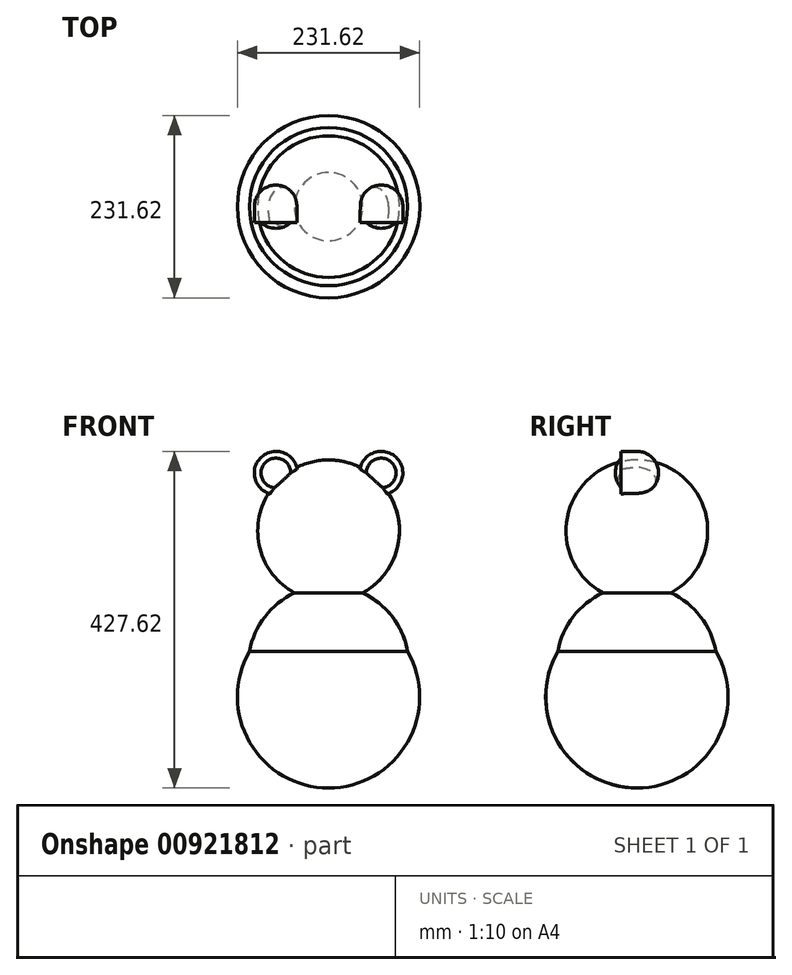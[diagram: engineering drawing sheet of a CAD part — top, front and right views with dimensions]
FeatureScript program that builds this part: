
annotation { "Feature Type Name" : "Feature", "Feature Type Description" : "" }
export const myFeature = defineFeature(function(context is Context, id is Id, definition is map)
    precondition{}
    {
        {
            var Q0;
            Q0=qCreatedBy(makeId("Front.planeOp"),FACE);
            var sketch = newSketch(context, id + "F0", { "sketchPlane" : qUnion([Q0])});
            skLineSegment(sketch, "E0", {"start": v(0, 115.17) * mm, "end": v(0, -108.63) * mm});
            skArc(sketch, "E1", {"start": v(0, 90) * mm, "mid": v(-90, 0) * mm, "end": v(0, -90) * mm});
            skSolve(sketch);
        }
        {
            var Q0;
            {var subQ0=sQuery(id+"F0.wireOp",EDGE,"mKIjtymj-Oh6m-so3v-0z2y-TkpC0XcMTjZ2");Q0=makeQuery(id+"F0.imprint","IMPRINT",FACE,{"disambiguationData":[TD([[makeQuery(id+"F0.imprint","IMPRINT",EDGE,{"derivedFrom":subQ0}),1.0]])]});}
            var Q1;
            {var subQ0=sQuery(id+"F0.wireOp",EDGE,"E1");Q1=makeQuery(id+"F0.imprint","IMPRINT",FACE,{"disambiguationData":[TD([[makeQuery(id+"F0.imprint","IMPRINT",EDGE,{"derivedFrom":subQ0}),1.0]])]});}
            var Q2;
            Q2=sQuery(id+"F0.wireOp",EDGE,"E0");
            revolve(context, id + "F1", {"surfaceOperationType" : NewSurfaceOperationType.NEW, "entities" : qUnion([Q0, Q1]), "axis" : qUnion([Q2]), "revolveType" : RevolveType.FULL});
        }
        {
            var Q0;
            Q0=qCreatedBy(makeId("Front.planeOp"),FACE);
            var sketch = newSketch(context, id + "F2", { "sketchPlane" : qUnion([Q0])});
            skCircle(sketch, "E2", {"center": v(-66.85, 73.44) * mm, "radius": 27.5 * mm});
            skLineSegment(sketch, "E3", {"start": v(0, 0) * mm, "end": v(0, 161.1) * mm});
            skCircle(sketch, "E4.MirrorC", {"center": v(66.85, 73.44) * mm, "radius": 27.5 * mm});
            skSolve(sketch);
        }
        {
            var Q0;
            Q0 = qSketchRegion(id + "F2", true);
            extrude(context, id + "F3", {"entities" : qUnion([Q0]), "operationType" : NewBodyOperationType.ADD, "depth" : 20 * mm, "offsetDistance" : 25 * mm});
        }
        {
            var Q0;
            Q0=makeQuery(id+"F3.opExtrude","CAP_FACE",FACE,{"disambiguationData":[OSD([sQuery(id+"F2.wireOp",EDGE,"E2")])],"isStart":true});
            var sketch = newSketch(context, id + "F4", { "sketchPlane" : qUnion([Q0])});
            skArc(sketch, "E5", {"start": v(66.85, 45.94) * mm, "mid": v(94.35, 73.44) * mm, "end": v(66.85, 100.94) * mm});
            skLineSegment(sketch, "E6", {"start": v(66.85, 126.85) * mm, "end": v(66.85, 15.2) * mm});
            skSolve(sketch);
        }
        {
            var Q0;
            Q0 = qSketchRegion(id + "F4", true);
            var Q1;
            Q1=sQuery(id+"F4.wireOp",EDGE,"E6");
            revolve(context, id + "F5", {"operationType" : NewBodyOperationType.ADD, "surfaceOperationType" : NewSurfaceOperationType.NEW, "entities" : qUnion([Q0]), "axis" : qUnion([Q1]), "revolveType" : RevolveType.FULL});
        }
        {
            var Q0;
            Q0=makeQuery(id+"F3.opExtrude","CAP_FACE",FACE,{"disambiguationData":[OSD([sQuery(id+"F2.wireOp",EDGE,"E4.MirrorC")])],"isStart":true});
            var sketch = newSketch(context, id + "F6", { "sketchPlane" : qUnion([Q0])});
            skArc(sketch, "E7", {"start": v(-66.85, 45.94) * mm, "mid": v(-39.35, 73.44) * mm, "end": v(-66.85, 100.94) * mm});
            skLineSegment(sketch, "E8", {"start": v(-66.85, 144.42) * mm, "end": v(-66.85, 14.63) * mm});
            skSolve(sketch);
        }
        {
            var Q0;
            Q0 = qSketchRegion(id + "F6", true);
            var Q1;
            Q1=sQuery(id+"F6.wireOp",EDGE,"E8");
            revolve(context, id + "F7", {"operationType" : NewBodyOperationType.ADD, "surfaceOperationType" : NewSurfaceOperationType.NEW, "entities" : qUnion([Q0]), "axis" : qUnion([Q1]), "revolveType" : RevolveType.FULL});
        }
        {
            var Q0;
            Q0=qCreatedBy(makeId("Right.planeOp"),FACE);
            var sketch = newSketch(context, id + "F8", { "sketchPlane" : qUnion([Q0])});
            skLineSegment(sketch, "E9", {"start": v(0, 0) * mm, "end": v(0, -69.2) * mm, "construction": true});
            skArc(sketch, "E10", {"start": v(100.46, -153.24) * mm, "mid": v(65.49, -92.98) * mm, "end": v(0, -69.2) * mm});
            skArc(sketch, "E11", {"start": v(0, -326.68) * mm, "mid": v(100.22, -268.92) * mm, "end": v(100.46, -153.24) * mm});
            skLineSegment(sketch, "E12", {"start": v(0, -69.2) * mm, "end": v(0, -326.68) * mm});
            skSolve(sketch);
        }
        {
            var Q0;
            Q0 = qSketchRegion(id + "F8", true);
            var Q1;
            Q1=sQuery(id+"F8.wireOp",EDGE,"E9");
            revolve(context, id + "F9", {"operationType" : NewBodyOperationType.ADD, "surfaceOperationType" : NewSurfaceOperationType.NEW, "entities" : qUnion([Q0]), "axis" : qUnion([Q1]), "revolveType" : RevolveType.FULL});
        }
    });
